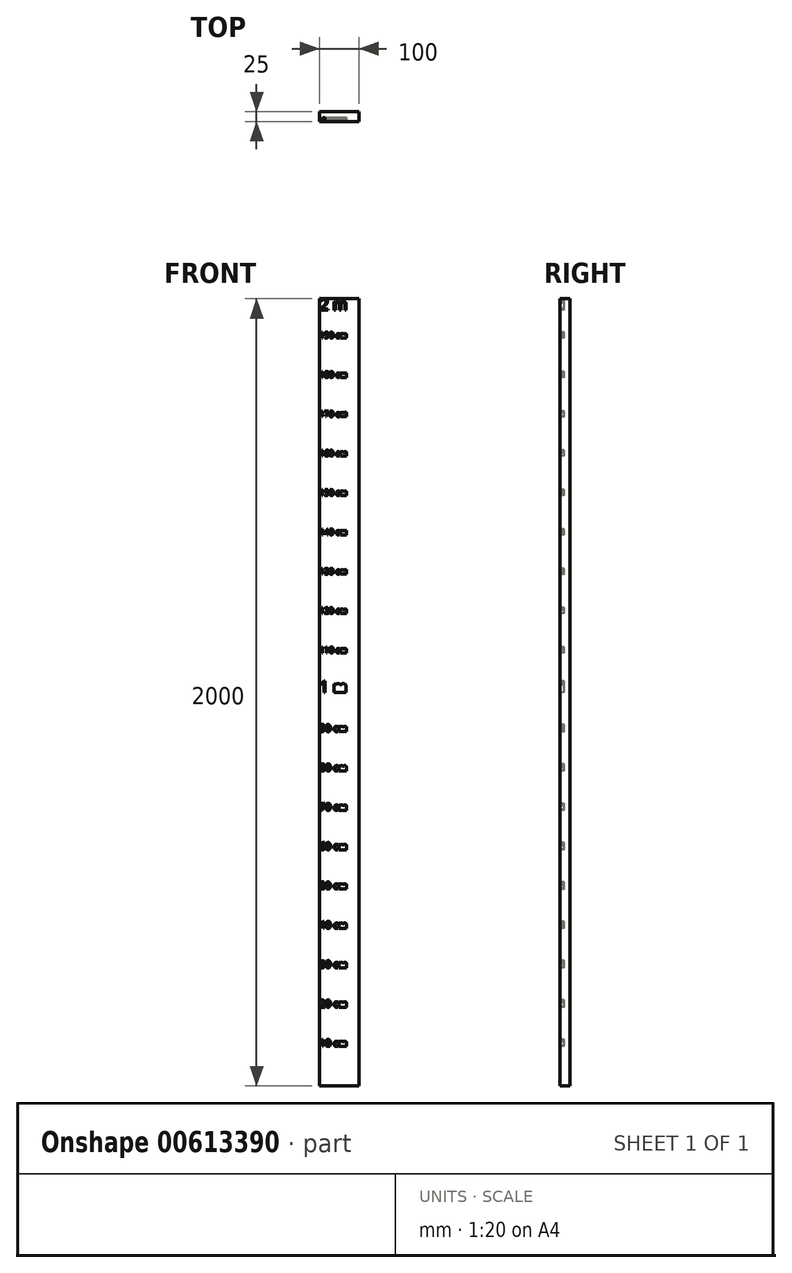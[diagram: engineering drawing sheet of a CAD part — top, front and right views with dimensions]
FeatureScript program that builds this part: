
annotation { "Feature Type Name" : "Feature", "Feature Type Description" : "" }
export const myFeature = defineFeature(function(context is Context, id is Id, definition is map)
    precondition{}
    {
        {
            var Q0;
            Q0=qCreatedBy(makeId("Front.planeOp"),FACE);
            var sketch = newSketch(context, id + "F0", { "sketchPlane" : qUnion([Q0])});
            skLineSegment(sketch, "E0.bottom", {"start": v(-61.66, -438.5) * mm, "end": v(38.34, -438.5) * mm});
            skLineSegment(sketch, "E0.top", {"start": v(-61.66, 1561.5) * mm, "end": v(38.34, 1561.5) * mm});
            skLineSegment(sketch, "E0.left", {"start": v(-61.66, -438.5) * mm, "end": v(-61.66, 1561.5) * mm});
            skLineSegment(sketch, "E0.right", {"start": v(38.34, -438.5) * mm, "end": v(38.34, 1561.5) * mm});
            skSolve(sketch);
        }
        {
            var Q0;
            Q0=makeQuery(id+"F0.imprint","IMPRINT",FACE,{"disambiguationData":[TD([[makeQuery(id+"F0.imprint","IMPRINT",EDGE,{"derivedFrom":sQuery(id+"F0.wireOp",EDGE,"E0.bottom")}),1.0]])]});
            extrude(context, id + "F1", {"entities" : qUnion([Q0]), "depth" : 25 * mm, "offsetDistance" : 25 * mm});
        }
        {
            var Q0;
            Q0=makeQuery(id+"F1.opExtrude","CAP_FACE",FACE,{"disambiguationData":[OSD([sQuery(id+"F0.wireOp",EDGE,"E0.bottom"),sQuery(id+"F0.wireOp",EDGE,"E0.top"),sQuery(id+"F0.wireOp",EDGE,"E0.left"),sQuery(id+"F0.wireOp",EDGE,"E0.right")])],"isStart":false});
            var sketch = newSketch(context, id + "F2", { "sketchPlane" : qUnion([Q0])});
            skLineSegment(sketch, "E1", {"start": v(-61.66, -338.5) * mm, "end": v(8.34, -338.5) * mm});
            skLineSegment(sketch, "E2.0.1.0", {"start": v(-61.66, -238.5) * mm, "end": v(8.34, -238.5) * mm});
            skLineSegment(sketch, "E2.0.2.0", {"start": v(-61.66, -138.5) * mm, "end": v(8.34, -138.5) * mm});
            skLineSegment(sketch, "E2.0.3.0", {"start": v(-61.66, -38.5) * mm, "end": v(8.34, -38.5) * mm});
            skLineSegment(sketch, "E2.0.4.0", {"start": v(-61.66, 61.5) * mm, "end": v(8.34, 61.5) * mm});
            skLineSegment(sketch, "E2.0.5.0", {"start": v(-61.66, 161.5) * mm, "end": v(8.34, 161.5) * mm});
            skLineSegment(sketch, "E2.0.6.0", {"start": v(-61.66, 261.5) * mm, "end": v(8.34, 261.5) * mm});
            skLineSegment(sketch, "E2.0.7.0", {"start": v(-61.66, 361.5) * mm, "end": v(8.34, 361.5) * mm});
            skLineSegment(sketch, "E2.0.8.0", {"start": v(-61.66, 461.5) * mm, "end": v(8.34, 461.5) * mm});
            skLineSegment(sketch, "E2.0.9.0", {"start": v(-61.66, 561.5) * mm, "end": v(8.34, 561.5) * mm});
            skLineSegment(sketch, "E2.0.10.0", {"start": v(-61.66, 661.5) * mm, "end": v(8.34, 661.5) * mm});
            skLineSegment(sketch, "E2.0.11.0", {"start": v(-61.66, 761.5) * mm, "end": v(8.34, 761.5) * mm});
            skLineSegment(sketch, "E2.0.12.0", {"start": v(-61.66, 861.5) * mm, "end": v(8.34, 861.5) * mm});
            skLineSegment(sketch, "E2.0.13.0", {"start": v(-61.66, 961.5) * mm, "end": v(8.34, 961.5) * mm});
            skLineSegment(sketch, "E2.0.14.0", {"start": v(-61.66, 1061.5) * mm, "end": v(8.34, 1061.5) * mm});
            skLineSegment(sketch, "E2.0.15.0", {"start": v(-61.66, 1161.5) * mm, "end": v(8.34, 1161.5) * mm});
            skLineSegment(sketch, "E2.0.16.0", {"start": v(-61.66, 1261.5) * mm, "end": v(8.34, 1261.5) * mm});
            skLineSegment(sketch, "E2.0.17.0", {"start": v(-61.66, 1361.5) * mm, "end": v(8.34, 1361.5) * mm});
            skLineSegment(sketch, "E2.0.18.0", {"start": v(-61.66, 1461.5) * mm, "end": v(8.34, 1461.5) * mm});
            skLineSegment(sketch, "E2.0.19.0", {"start": v(-61.66, 1561.5) * mm, "end": v(8.34, 1561.5) * mm});
            skLineSegment(sketch, "E2.direction1", {"start": v(-61.66, -338.5) * mm, "end": v(72, -300) * mm, "construction": true});
            skLineSegment(sketch, "E2.direction2", {"start": v(-61.66, -338.5) * mm, "end": v(-61.66, -238.5) * mm, "construction": true});
            skText(sketch, "E3", { "text": "10 cm", "fontName": "OpenSans-Regular.ttf"});
            skText(sketch, "E4", { "text": "20 cm", "fontName": "OpenSans-Regular.ttf"});
            skText(sketch, "E5", { "text": "30 cm", "fontName": "OpenSans-Regular.ttf"});
            skText(sketch, "E6", { "text": "40 cm", "fontName": "OpenSans-Regular.ttf"});
            skText(sketch, "E7", { "text": "50 cm", "fontName": "OpenSans-Regular.ttf"});
            skText(sketch, "E8", { "text": "60 cm", "fontName": "OpenSans-Regular.ttf"});
            skText(sketch, "E9", { "text": "70 cm", "fontName": "OpenSans-Regular.ttf"});
            skText(sketch, "E10", { "text": "80 cm", "fontName": "OpenSans-Regular.ttf"});
            skText(sketch, "E11", { "text": "90 cm", "fontName": "OpenSans-Regular.ttf"});
            skText(sketch, "E12", { "text": "1 m", "fontName": "OpenSans-Regular.ttf"});
            skText(sketch, "E13", { "text": "110 cm", "fontName": "OpenSans-Regular.ttf"});
            skText(sketch, "E14", { "text": "120 cm", "fontName": "OpenSans-Regular.ttf"});
            skText(sketch, "E15", { "text": "130 cm", "fontName": "OpenSans-Regular.ttf"});
            skText(sketch, "E16", { "text": "140 cm", "fontName": "OpenSans-Regular.ttf"});
            skText(sketch, "E17", { "text": "150 cm", "fontName": "OpenSans-Regular.ttf"});
            skText(sketch, "E18", { "text": "160 cm", "fontName": "OpenSans-Regular.ttf"});
            skText(sketch, "E19", { "text": "170 cm", "fontName": "OpenSans-Regular.ttf"});
            skText(sketch, "E20", { "text": "180 cm", "fontName": "OpenSans-Regular.ttf"});
            skText(sketch, "E21", { "text": "190 cm", "fontName": "OpenSans-Regular.ttf"});
            skText(sketch, "E22", { "text": "2 m", "fontName": "OpenSans-Regular.ttf"});
            const initialGuessF2  = {"E3": [-0.06166, -0.3385, 1, 0, 0.01804], "E4": [-0.06166, -0.2385, 1, 0, 0.01804], "E5": [-0.06166, -0.1385, 1, 0, 0.01804], "E6": [-0.06166, -0.0385, 1, 0, 0.01804], "E7": [-0.06166, 0.0615, 1, 0, 0.01804], "E8": [-0.06166, 0.1615, 1, 0, 0.01804], "E9": [-0.06166, 0.2615, 1, 0, 0.01804], "E10": [-0.06166, 0.3615, 1, 0, 0.01804], "E11": [-0.06166, 0.4615, 1, 0, 0.01804], "E12": [-0.06166, 0.5615, 1, 0, 0.02887], "E13": [-0.06166, 0.6615, 1, 0, 0.01498], "E14": [-0.06166, 0.7615, 1, 0, 0.01498], "E15": [-0.06166, 0.8615, 1, 0, 0.01498], "E16": [-0.06166, 0.9615, 1, 0, 0.01498], "E17": [-0.06166, 1.0615, 1, 0, 0.01498], "E18": [-0.06166, 1.1615, 1, 0, 0.01498], "E19": [-0.06166, 1.2615, 1, 0, 0.01498], "E20": [-0.06166, 1.3615, 1, 0, 0.01498], "E21": [-0.06166, 1.4615, 1, 0, 0.01498], "E22": [-0.06166, 1.53263, 1, 0, 0.02887]};
            skSetInitialGuess(sketch, initialGuessF2);
            skSolve(sketch);
        }
        {
            var Q0;
            Q0 = qSketchRegion(id + "F2", true);
            extrude(context, id + "F3", {"entities" : qUnion([Q0]), "operationType" : NewBodyOperationType.REMOVE, "oppositeDirection" : true, "depth" : 10 * mm, "offsetDistance" : 25 * mm});
        }
    });
